# Revit family: QF_Vollrath_FC-4C-03120-FAT
name_source: partatom
category: Specialty Equipment
revit_build: Autodesk Revit 2018 (Build: 20190510_1515(x64)
units: mm (PartAtom-declared; Revit-internal decimal feet)

## family parameters
Always vertical = Yes
Cut with Voids When Loaded = Yes
OmniClass Number = 23.40.40.14.24.14
OmniClass Title = Service Line Equipment
Part Type = Normal
Room Calculation Point = No
Round Connector Dimension = Use Diameter
Shared = No
Work Plane-Based = Yes

## types (1)
- QF_Vollrath_FC-4C-03120-FAT
    Apparent Power = 0 VA
    Assembly Code = E1090320
    BTUH = 4800.0 Btu/h
    CSI MasterFormat = 11 41 00
    Conn Plug = NEMA 5-15P
    Cycle = 60 Hz
    Default Elevation = 3' - 0"
    Description = Drop-In Cold Pan, Forced Air
    Elec Conn Connection Height = 0' - 2"
    FL Amps = 9 A
    Foodservice Equipment Identifier = Yes
    HP = 1/3
    Indirect Waste Connection Height = 0' - 2"
    Indirect Waste Size = 1"
    Manufacturer = Vollrath
    Model = FC-4C-03120-FA
    Phase = 1
    Refrigerant Type = R513A
    URL = https://www.vollrathfoodservice.com
    Volts = 120 V
    Weight in Pounds = 112

## geometry (parser evidence)
native form markers: Sweep x3
no freeform markers — native parametric forms only
